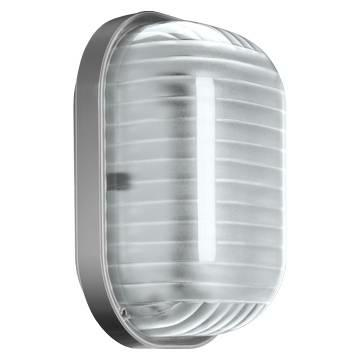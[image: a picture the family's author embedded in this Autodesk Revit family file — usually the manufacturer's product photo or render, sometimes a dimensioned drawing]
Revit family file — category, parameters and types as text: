
# Revit family: Lighting-Terziario-GEWISS-GUSCIO-PLAFONIERE-LED_COMPATTE_250
name_source: partatom
category: Apparecchi per illuminazione
revit_build: Autodesk Revit 2016 (Build: 20161004_0715(x64)
units: mm (PartAtom-declared; Revit-internal decimal feet)

## family parameters
Condiviso = No
Host = Superficie
Numero OmniClass = 23.80.00.00
Punto di calcolo locali = No
Quota connettore circolare = Usa diametro
Sorgente d'illuminazione = Sì
Taglio con vuoti quando caricato = No
Tipo di parte = Normale
Titolo OmniClass = Electric Power and Lighting

## types (6) — shared parameters
Angolo inclinazione = 0.00°
Applicazione = Interno / Esterno
Carico apparente = 60 VA
Catalogo = LIGHTING
Catalogo Serie = GUSCIO
Classe isolamento = II
Codice Electrocod = 2424
Emetti da lunghezza linea = 610 mm
File diagramma fotometrico = GW80601-80601358.IES
Filtro dei colori = 16777215
GEWISS - LED = GEWISS - Led - lm 650 / Temp_3000_K
GEWISS - STRUTTURA = GEWISS - Grigio RAL 7035
GEWISS - VETRO = GEWISS - vetro guscio
Glow Wire Test = 850°C
Grado di protezione = IP55
IDF = 68847c5d-753c-4d2f-a04e-8500da2b9afb
IDT = ee4907cc-fe26-4d18-ab55-b7b4fbf9869d
Immagine tipo = GW80771.jpg
Lampada = E27
Materiale = Policarbonato
Numero di poli = 2
Produttore = GEWISS S.p.A.
Prospetto di default = 1219 mm
Resistenza agli urti = IK10
Scheda Tecnica = https://www.gewiss.com
URL = https://www.gewiss.com
Variazione temperatura colore lampada con luminosità attenuata = <Nessuno>
Versione file RFA = 18.0
Voltaggio = 230 V

## per-type parameters (varying)
| type | Attacco lampada | Classe di efficienza lampada fornita | Codice EAN | Colore | Descrizione | Modello | Peso (kg) | Potenza lampada | Tensione | Tipo alimentatore | Tipo versione |
| GW80772 - Per lampada FSD 9W - Grigio grafite - IP55 | G23 | B ÷ A | 8011564210516 | Grigio grafite | GUSCIO 250x175 1X9W G23 IP55 GRIGIO GRAFITE | GW80772 | 0,9 |  | 230 V - 50 Hz | Reattore elettromagnetico KCG | Guscio 250 |
| GW80771 - Per lampada E27 60W - Grigio grafite - IP55 | E27 | D ÷ A+ | 8011564210509 | Grigio grafite | GUSCIO 250x175 60W E27 IP55 GRIGIO GRAFITE | GW80771 | 0,5 | 60W |  |  | Guscio 250 |
| GW80646 - Per lampada FSQ 13W - Grigio RAL 7035 - IP55 | G24q-1 | B ÷ A | 8011564183544 | Grigio RAL 7035 | GUSCIO 250x175 1x13W G24q-1 IP55 GRIGIO RAL7035 | GW80646 | 0,7 |  | 230 / 240 V - 50 / 60 Hz | Reattore elettronico EVG | Guscio 250 |
| GW80601 - Per lampada E27 60W - Grigio RAL 7035 - IP55 | E27 | D ÷ A+ | 8011564015180 | Grigio RAL 7035 | GUSCIO 250x175 60W E27 IP55 GRIGIO RAL7035 | GW80601 | 0,5 | 60W |  |  | Guscio 250 |
| GW80644 - Per lampada FSD 9W - Con crepusc. - Grigio RAL 7035 - IP55 | G23 | B ÷ A | 8011564034723 | Grigio RAL 7035 | GUSCIO 250x175 1X9W G23 INTERRUTTORE CREPUSCOLARE GRIGIO RAL7035 | GW80644 | 1 |  | 230 V - 50 Hz | Reattore elettromagnetico KCG | Guscio 250 - Con interruttore crepuscolare |
| GW80604 - Per lampada FSD 9W - Grigio RAL 7035 - IP55 | G23 | B ÷ A | 8011564015210 | Grigio RAL 7035 | GUSCIO 250x175 1X9W G23 IP55 GRIGIO RAL7035 | GW80604 | 0,9 |  | 230 V - 50 Hz | Reattore elettromagnetico KCG | Guscio 250 |
